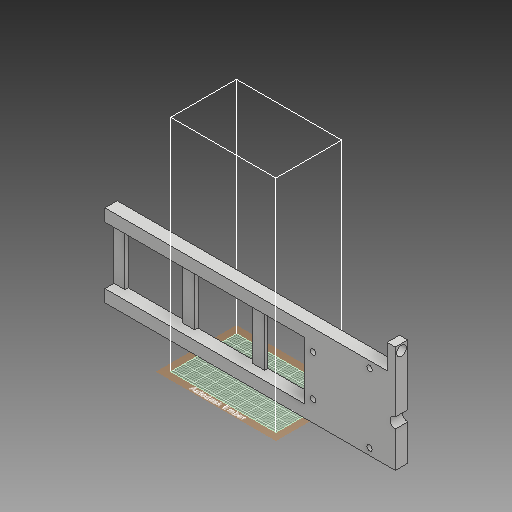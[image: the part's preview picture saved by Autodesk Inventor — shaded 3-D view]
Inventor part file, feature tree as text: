
AUTODESK INVENTOR PART (.ipt)
format: ipt  version: 2018 (Build 220112000, 112)  size: 1,021,440 bytes
history: native  units: mm
features: sketch x68, extrude x55, fillet x18, hole x8
ambient origin geometry x8: Origin, YZ Plane, XZ Plane, XY Plane, X Axis, Y Axis, Z Axis, Center Point
bodies: Solid1 (feature_tree)
feature tree (149):
  extrude  "Extrusion1"  Depth=50.0mm
  hole  "Hole1"  [1 undecoded]
  hole  "Hole2"  [1 undecoded]
  extrude  "Extrusion2"  Depth=25.0mm
  extrude  "Extrusion3"  Depth=25.0mm
  extrude  "Extrusion4"  Depth=5.0mm
  sketch  "Sketch7"  dims[d25=10.0mm d26=5.0mm]
  extrude  "Extrusion5"  Depth=10.0mm
  extrude  "Extrusion6"  Depth=35.0mm
  extrude  "Extrusion7"  Depth=35.0mm
  extrude  "Extrusion8"  Depth=35.0mm
  extrude  "Extrusion9"  Depth=2.0mm TaperAngle=0.0deg
  extrude  "Extrusion10"  Depth=10.0mm TaperAngle=0.0deg
  extrude  "Extrusion11"  Depth=10.0mm
  extrude  "Extrusion12"  Depth=7.5mm
  fillet  "Fillet1"  Radius=7.5mm
  fillet  "Fillet2"  Radius=25.0mm
  fillet  "Fillet3"  Radius=3.0mm
  fillet  "Fillet4"  Radius=3.2mm
  fillet  "Fillet5"  Radius=2.1mm
  fillet  "Fillet6"  Radius=5.5mm
  extrude  "Extrusion13"  Depth=92.5mm TaperAngle=0.0deg
  sketch  "Sketch17"  dims[d58=4.25mm d59=241.0mm d60=0.0mm]
  hole  "Hole3"  [1 undecoded]
  hole  "Hole4"  [1 undecoded]
  extrude  "Extrusion14"  Depth=5.0mm
  extrude  "Extrusion15"  Depth=2.5mm TaperAngle=0.0deg
  extrude  "Extrusion16"  Depth=6.35mm
  extrude  "Extrusion17"  Depth=2.5mm
  extrude  "Extrusion18"  Depth=14.55mm TaperAngle=0.0deg
  extrude  "Extrusion19"  Depth=0.1mm
  extrude  "Extrusion20"  Depth=3.25mm
  extrude  "Extrusion21"  Depth=3.25mm
  hole  "Hole5"  [1 undecoded]
  extrude  "Extrusion22"  Depth=3.6mm
  extrude  "Extrusion23"  Depth=6.0mm
  extrude  "Extrusion24"  Depth=10.0mm TaperAngle=0.0deg
  hole  "Hole6"  [1 undecoded]
  extrude  "Extrusion25"  Depth=100.0mm TaperAngle=0.0deg
  extrude  "Extrusion26"  Depth=2.0mm TaperAngle=0.0deg
  extrude  "Extrusion27"  Depth=3.3mm
  extrude  "Extrusion28"  Depth=3.3mm
  hole  "Hole7"  [1 undecoded]
  extrude  "Extrusion29"  Depth=42.0mm
  extrude  "Extrusion30"  Depth=21.0mm
  hole  "Hole8"  [1 undecoded]
  extrude  "Extrusion31"  Depth=21.0mm
  extrude  "Extrusion32"  Depth=10.0mm
  fillet  "Fillet7"  Radius=3.3mm
  fillet  "Fillet8"  Radius=10.0mm
  extrude  "Extrusion33"  Depth=5.0mm
  extrude  "Extrusion34"  Depth=10.0mm
  sketch  "Sketch45"  dims[d149=10.0mm d150=17.5mm d151=0.0mm]
  sketch  "Sketch46"  dims[d152=5.0mm]
  extrude  "Extrusion35"  Depth=10.0mm TaperAngle=0.0deg
  extrude  "Extrusion36"  Depth=17.5mm TaperAngle=0.0deg
  extrude  "Extrusion37"  Depth=3.75mm
  extrude  "Extrusion38"  Depth=3.75mm
  extrude  "Extrusion39"  Depth=10.0mm TaperAngle=0.0deg
  extrude  "Extrusion40"  Depth=2.0mm TaperAngle=0.0deg
  fillet  "Fillet9"  Radius=5.0mm
  fillet  "Fillet10"  Radius=15.0mm
  fillet  "Fillet11"  Radius=7.5mm
  fillet  "Fillet12"  Radius=17.5mm
  extrude  "Extrusion41"  Depth=47.5mm
  extrude  "Extrusion42"  Depth=5.0mm
  sketch  "Sketch55"  dims[d200=20.0mm d203=5.0mm]
  extrude  "Extrusion43"  Depth=29.0mm
  extrude  "Extrusion44"  Depth=7.5mm TaperAngle=0.0deg
  extrude  "Extrusion45"  Depth=4.0mm
  extrude  "Extrusion46"  Depth=12.0mm
  extrude  "Extrusion47"  Depth=7.5mm
  extrude  "Extrusion48"  Depth=20.0mm TaperAngle=0.0deg
  extrude  "Extrusion49"  Depth=3.3mm
  extrude  "Extrusion50"  Depth=4.0mm
  extrude  "Extrusion51"  Depth=10.0mm TaperAngle=0.0deg
  extrude  "Extrusion52"  Depth=10.0mm TaperAngle=0.0deg
  fillet  "Fillet13"  Radius=10.0mm
  fillet  "Fillet14"  Radius=74.724mm
  fillet  "Fillet15"  Radius=74.724mm
  fillet  "Fillet16"  Radius=85.515mm
  extrude  "Extrusion53"  Depth=5.0mm
  extrude  "Extrusion54"  Depth=5.0mm
  fillet  "Fillet17"  Radius=85.515mm
  extrude  "Extrusion55"  Depth=1.0mm TaperAngle=0.0deg
  fillet  "Fillet18"  Radius=2.0mm
  sketch  "Sketch1"  dims[d0=50.0mm d1=50.0mm]
  sketch  "Sketch2"  dims[d2=240.0mm d3=7.5mm]
  sketch  "Sketch3"  dims[d4=7.5mm d5=7.5mm d6=0.0mm]
  sketch  "Sketch4"  dims[d7=6.35mm d8=6.0mm d9=4.0mm d10=2.0mm d11=90.0deg d12=8.0mm d13=20.594885mm d14=25.0mm]
  sketch  "Sketch5"  dims[d15=3.3mm d16=6.0mm d17=4.0mm d18=2.0mm d19=90.0deg d20=8.0mm d21=20.594885mm d22=25.0mm]
  sketch  "Sketch6"  dims[d23=180.0deg d24=5.0mm]
  sketch  "Sketch8"  dims[d27=17.5mm d28=0.0mm d30=35.0mm]
  sketch  "Sketch9"  dims[d31=35.0mm d32=35.0mm]
  sketch  "Sketch10"  dims[d33=35.0mm d34=35.0mm]
  sketch  "Sketch11"  dims[d35=35.0mm d36=2.0mm d37=0.0mm]
  sketch  "Sketch12"  dims[d38=10.0mm d39=7.5mm d40=0.0mm]
  sketch  "Sketch13"  dims[d41=100.0mm d42=10.0mm]
  sketch  "Sketch14"  dims[d43=7.5mm d44=0.0mm d45=7.5mm d46=7.5mm d47=25.0mm d48=0.0mm d49=3.0mm d50=3.2mm d51=2.1mm d52=5.5mm]
  sketch  "Sketch15"  dims[d53=3.3mm d54=92.5mm d55=0.0mm]
  sketch  "Sketch16"  dims[d56=5.5mm d57=3.3mm]
  sketch  "Sketch18"  dims[d61=4.44mm d62=5.0mm]
  sketch  "Sketch19"  dims[d63=2.5mm d64=91.25mm d65=0.0mm]
  sketch  "Sketch20"  dims[d66=30.0mm d67=6.35mm]
  sketch  "Sketch21"  dims[d68=3.8mm d69=0.0mm d70=2.5mm]
  sketch  "Sketch22"  dims[d71=14.55mm d72=0.0mm d73=14.55mm d74=0.0mm]
  sketch  "Sketch23"  dims[d75=0.1mm d76=0.1mm]
  sketch  "Sketch24"  dims[d77=3.25mm d78=3.25mm]
  sketch  "Sketch25"  dims[d79=3.25mm d80=3.25mm]
  sketch  "Sketch26"  dims[d81=35.0mm d82=10.0mm]
  sketch  "Sketch27"  dims[d83=2.0mm d84=0.0mm d85=3.6mm]
  sketch  "Sketch28"  dims[d86=3.6mm]
  sketch  "Sketch29"  dims[d87=3.3mm d88=6.0mm d89=4.0mm d90=2.0mm d91=90.0deg d92=15.0mm d93=20.594885mm]
  sketch  "Sketch30"  dims[d94=3.3mm d95=6.0mm d96=4.0mm d97=2.0mm d98=90.0deg d99=15.0mm d100=20.594885mm d101=6.0mm]
  sketch  "Sketch31"  dims[d102=20.0mm d103=0.0mm d104=10.0mm d105=0.0mm]
  sketch  "Sketch32"  dims[d106=2.0mm d107=0.0mm d108=4.0mm]
  sketch  "Sketch33"  dims[d109=100.0mm d110=0.0mm d111=100.0mm d112=0.0mm]
  sketch  "Sketch34"  dims[d113=5.0mm d114=2.0mm d115=0.0mm]
  sketch  "Sketch35"  dims[d116=3.3mm d117=3.3mm]
  sketch  "Sketch36"  dims[d118=3.3mm d119=3.3mm]
  sketch  "Sketch37"  dims[d120=2.0mm d121=0.0mm d122=5.5mm d123=0.0mm]
  sketch  "Sketch38"  dims[d124=3.3mm d125=6.0mm d126=4.0mm d127=2.0mm d128=90.0deg d129=8.0mm d130=20.594885mm d131=42.0mm]
  sketch  "Sketch39"  dims[d132=17.0mm d133=21.0mm]
  sketch  "Sketch40"  dims[d135=8.5mm d136=15.825mm]
  sketch  "Sketch41"  dims[d137=3.5mm d138=21.0mm]
  sketch  "Sketch42"  dims[d139=3.3mm d140=3.3mm d141=3.3mm d142=10.0mm d143=0.0mm]
  sketch  "Sketch43"  dims[d144=7.5mm d145=0.0mm d146=5.0mm]
  sketch  "Sketch44"  dims[d147=10.0mm d148=5.0mm]
  sketch  "Sketch47"  dims[d153=7.0mm d154=6.0mm d155=4.0mm d156=2.0mm d157=90.0deg d158=8.0mm d159=20.594885mm d160=17.5mm d161=0.0mm]
  sketch  "Sketch48"  dims[d162=170.5mm d163=0.0mm d164=3.75mm]
  sketch  "Sketch49"  dims[d165=3.75mm d166=3.75mm]
  sketch  "Sketch50"  dims[d167=3.75mm d168=10.0mm d169=0.0mm]
  sketch  "Sketch51"  dims[d170=100.0mm d171=0.0mm]
  sketch  "Sketch52"  dims[d172=5.0mm d173=6.0mm d174=4.0mm d175=2.0mm d176=90.0deg d177=15.0mm d178=0.0mm d179=2.0mm d180=0.0mm d181=5.0mm d182=15.0mm d183=0.0mm d184=7.5mm]
  sketch  "Sketch53"  dims[d185=6.0mm d186=6.0mm d187=4.0mm d188=2.0mm d189=90.0deg d190=15.0mm d191=0.0mm d192=17.5mm d193=0.0mm]
  sketch  "Sketch54"  dims[d194=23.75mm d195=47.5mm]
  sketch  "Sketch56"  dims[d204=5.0mm d205=29.0mm]
  sketch  "Sketch57"  dims[d206=29.0mm d207=7.5mm d208=0.0mm]
  sketch  "Sketch58"  dims[d209=4.0mm d210=4.0mm]
  sketch  "Sketch59"  dims[d211=2.0mm d212=0.0mm d213=12.0mm]
  sketch  "Sketch60"  dims[d214=2.0mm d215=0.0mm d216=7.5mm]
  sketch  "Sketch61"  dims[d217=7.5mm d218=20.0mm d219=0.0mm]
  sketch  "Sketch62"  dims[d220=20.0mm d221=3.3mm]
  sketch  "Sketch63"  dims[d222=20.0mm d223=0.0mm d224=4.0mm]
  sketch  "Sketch64"  dims[d225=4.0mm d226=10.0mm d227=0.0mm]
  sketch  "Sketch65"  dims[d228=3.0mm d229=5.5mm d230=0.0mm d231=10.0mm d232=0.0mm d233=74.724mm d234=74.724mm d235=85.515mm]
  sketch  "Sketch66"  dims[d236=5.0mm d237=5.0mm]
  sketch  "Sketch67"  dims[d238=85.515mm d239=5.0mm d240=85.515mm]
  sketch  "Sketch68"  dims[d241=5.0mm d242=2.0mm d243=0.0mm d244=2.0mm d245=2.0mm d246=2.0mm d247=2.0mm d248=10.0mm d249=2.0mm d250=0.0mm d251=1.0mm d252=0.0mm d253=20.0mm d254=1.0mm d255=0.0mm d256=0.5mm d257=0.0mm d258=0.349066mm d259=0.349066mm d260=4.0mm d261=4.0mm d262=4.0mm d263=10.0mm d264=0.0mm d265=5.5mm d266=0.0mm d267=6.5mm d268=5.5mm d269=0.0mm d270=3.0mm d271=24.5mm d272=5500.0mm d273=0.0mm d274=5500.0mm d275=0.0mm d276=24.5mm d277=7.5mm d278=0.0mm d279=7.5mm d280=0.0mm d281=7.5mm d282=0.0mm d283=2.0mm d284=2.0mm d285=4.0mm d286=1.5mm d287=4.25mm d288=4.25mm d289=7.5mm d290=0.0mm d291=20.025mm d292=10.0mm d293=2.5mm d294=17.0mm d295=0.0mm d296=1.5mm d298=3.0mm d300=3.0mm d301=5.0mm d302=0.0mm d303=1.0mm]
note: 8 required parameter values undecoded (feature->parameter linkage not recoverable at this tier; creation-order binding heuristic only, values carry confidence <= 0.55)
